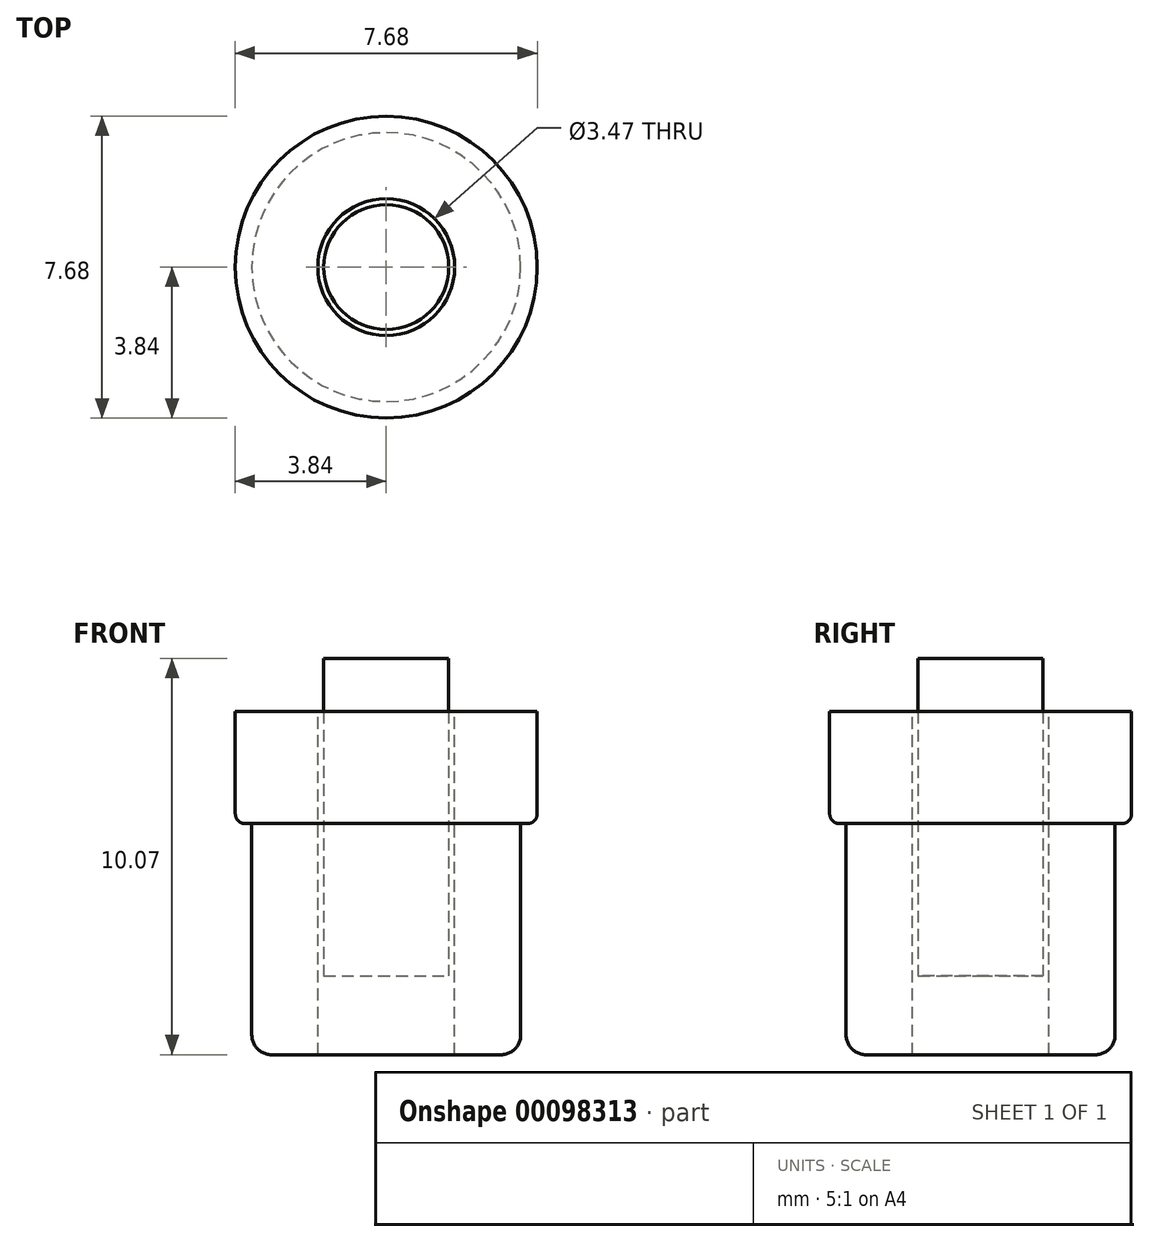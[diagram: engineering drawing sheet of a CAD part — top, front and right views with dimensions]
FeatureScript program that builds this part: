
annotation { "Feature Type Name" : "Feature", "Feature Type Description" : "" }
export const myFeature = defineFeature(function(context is Context, id is Id, definition is map)
    precondition{}
    {
        {
            var Q0;
            Q0=qCreatedBy(makeId("Front.planeOp"),FACE);
            var sketch = newSketch(context, id + "F0", { "sketchPlane" : qUnion([Q0])});
            skLineSegment(sketch, "E0", {"start": v(0, 0) * mm, "end": v(-3.42, 0) * mm});
            skLineSegment(sketch, "E1", {"start": v(-3.42, 0) * mm, "end": v(-3.42, 5.87) * mm});
            skLineSegment(sketch, "E2", {"start": v(-3.42, 5.87) * mm, "end": v(-3.84, 5.87) * mm});
            skLineSegment(sketch, "E3", {"start": v(-3.84, 5.87) * mm, "end": v(-3.84, 8.72) * mm});
            skLineSegment(sketch, "E4", {"start": v(-3.84, 8.72) * mm, "end": v(-1.74, 8.72) * mm});
            skLineSegment(sketch, "E5", {"start": v(-1.74, 8.72) * mm, "end": v(-1.74, 2) * mm});
            skLineSegment(sketch, "E6", {"start": v(-1.74, 2) * mm, "end": v(0, 2) * mm});
            skLineSegment(sketch, "E7", {"start": v(0, 2) * mm, "end": v(0, 0) * mm});
            skSolve(sketch);
        }
        {
            var Q0;
            Q0=qSketchRegion(id+"F0",true);
            var Q1;
            Q1=sQuery(id+"F0.wireOp",EDGE,"E7");
            revolve(context, id + "F1", {"entities" : qUnion([Q0]), "axis" : qUnion([Q1]), "revolveType" : RevolveType.FULL});
        }
        {
            var Q0;
            Q0=makeQuery(id+"F1.opRevolve","SWEPT_EDGE",EDGE,{"disambiguationData":[OSD([sQuery(id+"F0.wireOp",EDGE,"E2"),sQuery(id+"F0.wireOp",EDGE,"E3")])]});
            fillet(context, id + "F2", {"entities" : qUnion([Q0]), "radius" : 0.25 * mm, "allowEdgeOverflow" : false});
        }
        {
            var Q0;
            Q0=makeQuery(id+"F1.opRevolve","SWEPT_EDGE",EDGE,{"disambiguationData":[OSD([sQuery(id+"F0.wireOp",EDGE,"E0"),sQuery(id+"F0.wireOp",EDGE,"E1")])]});
            fillet(context, id + "F3", {"entities" : qUnion([Q0]), "radius" : 0.5 * mm, "allowEdgeOverflow" : false});
        }
        {
            var Q0;
            Q0=qCreatedBy(makeId("Front.planeOp"),FACE);
            var sketch = newSketch(context, id + "F4", { "sketchPlane" : qUnion([Q0])});
            skLineSegment(sketch, "E8.bottom", {"start": v(0, 0) * mm, "end": v(-1.59, 0) * mm});
            skLineSegment(sketch, "E8.top", {"start": v(0, 10.07) * mm, "end": v(-1.59, 10.07) * mm});
            skLineSegment(sketch, "E8.left", {"start": v(0, 0) * mm, "end": v(0, 10.07) * mm});
            skLineSegment(sketch, "E8.right", {"start": v(-1.59, 0) * mm, "end": v(-1.59, 10.07) * mm});
            skSolve(sketch);
        }
        {
            var Q0;
            Q0=qSketchRegion(id+"F4",true);
            var Q1;
            Q1=sQuery(id+"F4.wireOp",EDGE,"E8.left");
            revolve(context, id + "F5", {"entities" : qUnion([Q0]), "axis" : qUnion([Q1]), "revolveType" : RevolveType.FULL});
        }
        {
            var Q0;
            Q0=makeQuery(id+"F1.opRevolve","SWEPT_FACE",FACE,{"disambiguationData":[OSD([sQuery(id+"F0.wireOp",EDGE,"E6")])]});
            var Q1;
            Q1=makeQuery(id+"F1.opRevolve","SWEPT_FACE",FACE,{"disambiguationData":[OSD([sQuery(id+"F0.wireOp",EDGE,"E0")])]});
            extrude(context, id + "F6", {"entities" : qUnion([Q0]), "operationType" : NewBodyOperationType.REMOVE, "endBound" : BoundingType.UP_TO_SURFACE, "oppositeDirection" : true, "endBoundEntityFace" : qUnion([Q1]), "depth" : 25 * mm});
        }
    });
